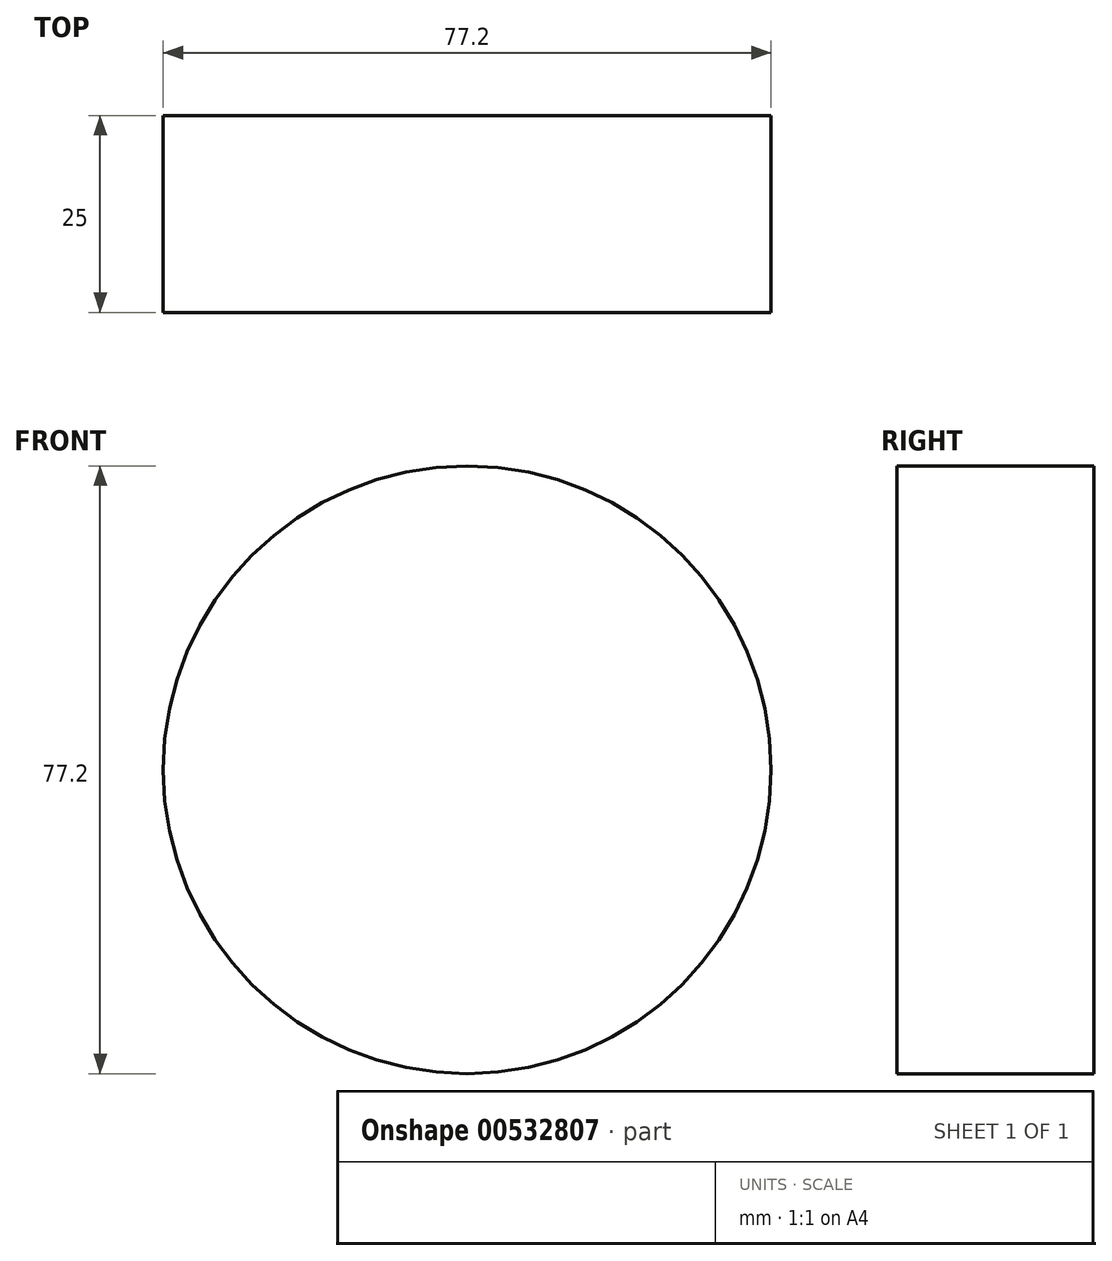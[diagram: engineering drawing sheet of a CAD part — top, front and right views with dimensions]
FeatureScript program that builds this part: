
annotation { "Feature Type Name" : "Feature", "Feature Type Description" : "" }
export const myFeature = defineFeature(function(context is Context, id is Id, definition is map)
    precondition{}
    {
        {
            var Q0;
            Q0=qCreatedBy(makeId("Front.planeOp"),FACE);
            var sketch = newSketch(context, id + "F0", { "sketchPlane" : qUnion([Q0])});
            skCircle(sketch, "E0", {"center": v(0, 0) * mm, "radius": 38.6 * mm});
            skSolve(sketch);
        }
        {
            var Q0;
            Q0=makeQuery(id+"F0.imprint","IMPRINT",FACE,{"disambiguationData":[TD([[makeQuery(id+"F0.imprint","IMPRINT",EDGE,{"derivedFrom":sQuery(id+"F0.wireOp",EDGE,"E0")}),1.0]])]});
            extrude(context, id + "F1", {"entities" : qUnion([Q0]), "depth" : 25 * mm, "offsetDistance" : 25 * mm});
        }
    });
